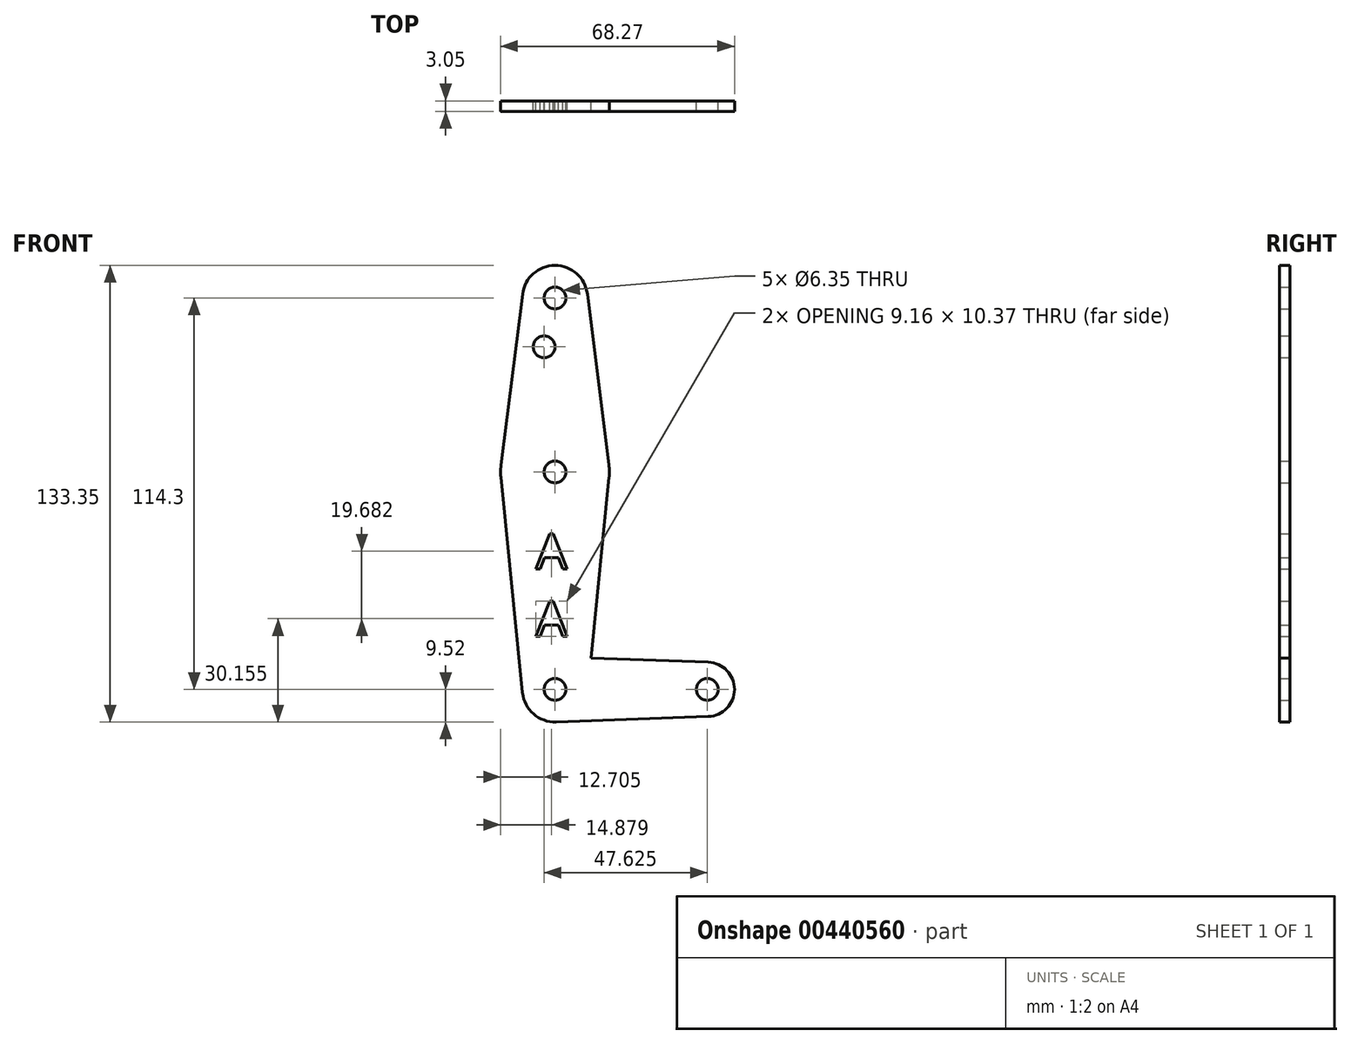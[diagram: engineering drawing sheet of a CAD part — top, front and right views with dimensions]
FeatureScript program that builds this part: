
annotation { "Feature Type Name" : "Feature", "Feature Type Description" : "" }
export const myFeature = defineFeature(function(context is Context, id is Id, definition is map)
    precondition{}
    {
        {
            var Q0;
            Q0=qCreatedBy(makeId("Front.planeOp"),FACE);
            var sketch = newSketch(context, id + "F0", { "sketchPlane" : qUnion([Q0])});
            skLineSegment(sketch, "E0", {"start": v(0, 114.3) * mm, "end": v(0, 0) * mm, "construction": true});
            skLineSegment(sketch, "E1", {"start": v(0, 0) * mm, "end": v(44.45, 0) * mm, "construction": true});
            skCircle(sketch, "E2", {"center": v(0, 0) * mm, "radius": 9.53 * mm});
            skCircle(sketch, "E3", {"center": v(44.45, 0) * mm, "radius": 7.94 * mm});
            skCircle(sketch, "E4", {"center": v(0, 63.5) * mm, "radius": 15.88 * mm});
            skCircle(sketch, "E5", {"center": v(0, 114.3) * mm, "radius": 9.53 * mm});
            skLineSegment(sketch, "E6", {"start": v(15.8, 61.91) * mm, "end": v(9.48, -0.95) * mm});
            skLineSegment(sketch, "E7", {"start": v(-15.8, 61.91) * mm, "end": v(-9.48, -0.95) * mm});
            skLineSegment(sketch, "E8", {"start": v(15.75, 65.48) * mm, "end": v(9.45, 115.5) * mm});
            skLineSegment(sketch, "E9", {"start": v(-9.45, 115.5) * mm, "end": v(-15.75, 65.48) * mm});
            skLineSegment(sketch, "E10", {"start": v(44.73, 7.93) * mm, "end": v(0.34, 9.52) * mm});
            skLineSegment(sketch, "E11", {"start": v(44.73, -7.93) * mm, "end": v(0, -9.53) * mm});
            skCircle(sketch, "E12", {"center": v(0, 114.3) * mm, "radius": 3.18 * mm});
            skCircle(sketch, "E13", {"center": v(0, 63.5) * mm, "radius": 3.18 * mm});
            skCircle(sketch, "E14", {"center": v(0, 0) * mm, "radius": 3.18 * mm});
            skCircle(sketch, "E15", {"center": v(44.45, 0) * mm, "radius": 3.18 * mm});
            skCircle(sketch, "E16", {"center": v(-3.17, 100.03) * mm, "radius": 3.18 * mm});
            skText(sketch, "E17", { "text": "A\nA", "fontName": "OpenSans-Regular.ttf"});
            const initialGuessF0  = {"E17": [-0.00558, 0.03513, 1, 0, 0.01042]};
            skSetInitialGuess(sketch, initialGuessF0);
            skSolve(sketch);
        }
        {
            var Q0;
            Q0 = qSketchRegion(id + "F0", true);
            extrude(context, id + "F1", {"entities" : qUnion([Q0]), "depth" : 3.05 * mm});
        }
    });
